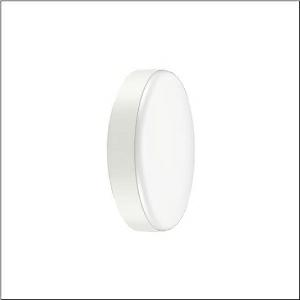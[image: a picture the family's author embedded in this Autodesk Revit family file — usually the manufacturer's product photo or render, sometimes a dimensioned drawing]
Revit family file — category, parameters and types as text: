
# Revit family: round_31_51wc10mb34as
name_source: partatom
category: Lighting Fixtures
units: mm (PartAtom-declared; Revit-internal decimal feet)

## family parameters
Cut with Voids When Loaded = No
Host = Face
Light Source = No
Part Type = Normal
Room Calculation Point = No
Round Connector Dimension = Use Diameter
Shared = No

## types (1)
- --- (1 x LED, 4250 lm, 35.4 W, 3000K)
    Apparent Load = 35 VA
    CIE Flux Codes = 44 75 94 94 100
    Color Rendering = 80
    Color Temperature = 3000K
    Default Elevation = 1800 mm
    Description = Round 31, wall and ceiling luminaire, primary optical cover: cover, of PC, opal, light emission: direct distribution, primary light characteristic: symmetric, installation type: surface-mounted, LED, rated luminous flux: 4.250lm, luminous efficacy: 120lm/W, light colour: 830, colour temperature: 3000K, control gear: ON/OFF Multilumen, with terminal, 3-pole, max. 2.5mm², mains connection: 220..240V, AC, 50/60Hz, rated input power: 35W, luminaire housing, of PC, traffic white (RAL 9016), diameter: 480mm, brightness and presence sensor, HF sensor, protection rating (complete): IP65, insulation class (complete): insulation class II (safety insulation), certification: CE, impact resistance: IK10, permissible operating ambient temperature: -20..+40°C, permissible storage temperature: -20..+60°C, packaging unit: 1 piece
    Height = 97 mm
    Lamp = 1 x LED
    Lamp Light Flux = 4250 lm
    Lamp Power = 35.4 W
    Lamp count = 1
    Length = 480 mm
    Luminous efficacy = 120 lm/W
    Manufacturer = Siteco
    ModVariant = No
    Model = 51WC10MB34AS
    Mounting Place = Ceiling
    Mounting Type = Surface mounted
    Number of Poles = 1
    OnlyDefault = Yes
    Power Factor = 1
    Product Name = Round 31
    Product group = wall and ceiling luminaire
    ProductGroupID = 304
    Protection Class = Protection class II
    Protection Degree = IP 65
    RLX_Detail_Level = 1
    RLX_Emergency_Light_Flux = 0 lm
    RLX_Emergency_Type = 0
    RLX_Emergency_Type_DB = No
    RlxData = <blob elided: 41385 chars, md5=d1b7092c>
    Socket = socket
    Standby Power = 0 W
    System Light Flux = 4250 lm
    System Power = 35 W
    Type Comments = factory setting: luminous flux: 100 % | (ON | ON)
    Type Image = l_1007188.jpg
    URL = http://relux.com
    VarID = @adj_111850
    Voltage = 0 V
    Weight = 0.00 kg
    Width = 0 mm  [stored 0 ft]

note: [stored X ft] marks values corroborated as IEEE doubles in the binary element streams (Revit-internal decimal feet)

## geometry (parser evidence)
native form markers: Blend x4, Sweep x13
no freeform markers — native parametric forms only
